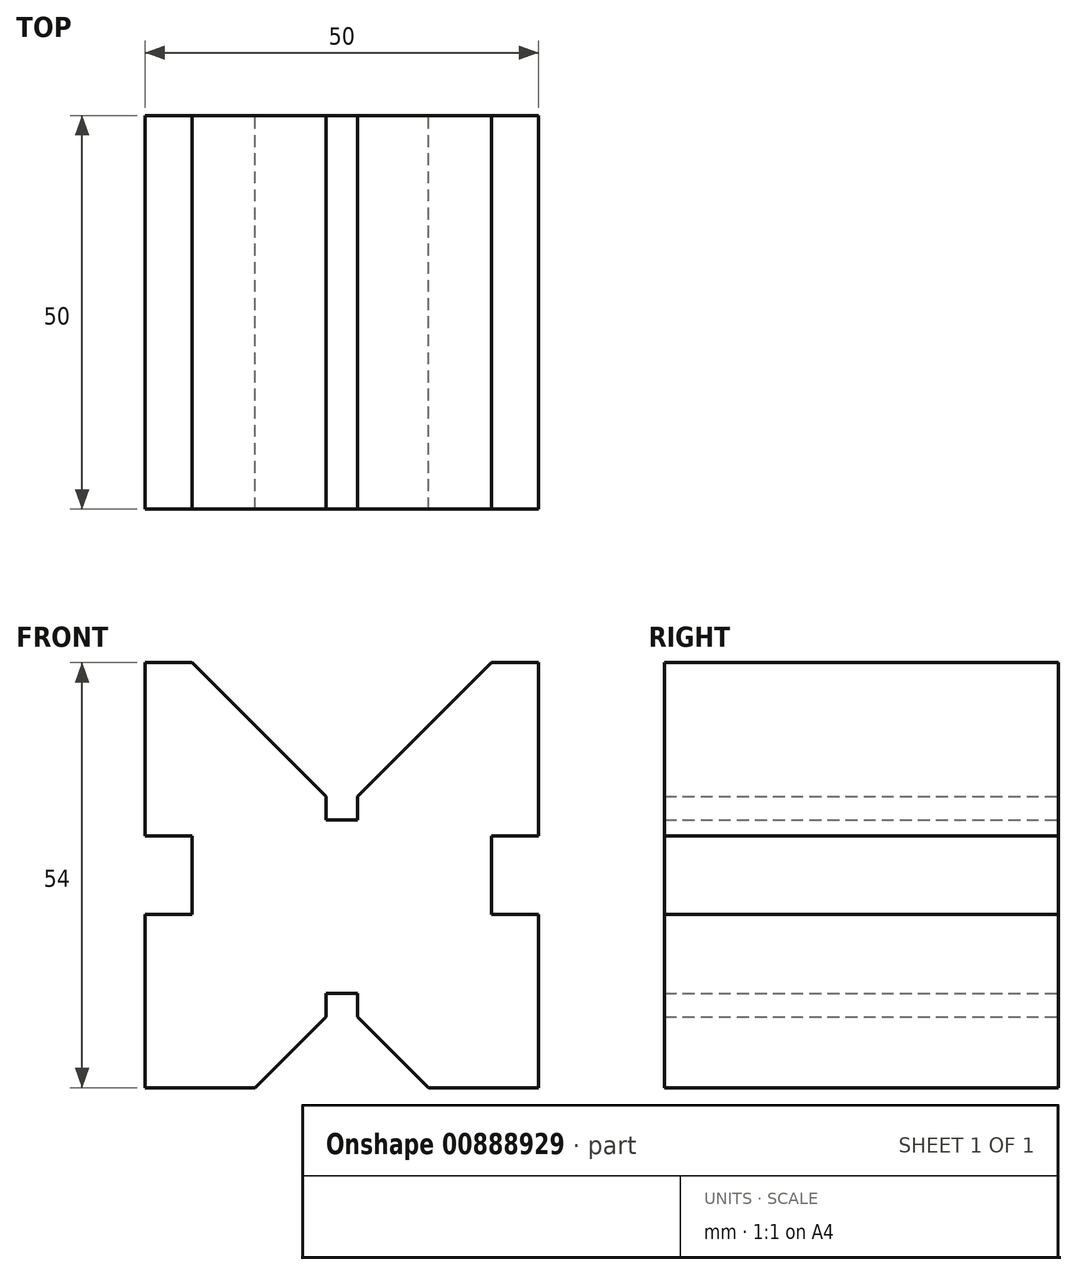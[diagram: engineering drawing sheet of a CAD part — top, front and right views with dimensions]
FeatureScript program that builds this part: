
annotation { "Feature Type Name" : "Feature", "Feature Type Description" : "" }
export const myFeature = defineFeature(function(context is Context, id is Id, definition is map)
    precondition{}
    {
        {
            var Q0;
            Q0=qCreatedBy(makeId("Front.planeOp"),FACE);
            var sketch = newSketch(context, id + "F0", { "sketchPlane" : qUnion([Q0])});
            skLineSegment(sketch, "E0", {"start": v(-6, 54) * mm, "end": v(0, 54) * mm});
            skLineSegment(sketch, "E1", {"start": v(0, 54) * mm, "end": v(0, 32) * mm});
            skLineSegment(sketch, "E2", {"start": v(0, 32) * mm, "end": v(-6, 32) * mm});
            skLineSegment(sketch, "E3", {"start": v(-6, 32) * mm, "end": v(-6, 22) * mm});
            skLineSegment(sketch, "E4", {"start": v(-6, 22) * mm, "end": v(0, 22) * mm});
            skLineSegment(sketch, "E5", {"start": v(0, 22) * mm, "end": v(0, 0) * mm});
            skLineSegment(sketch, "E6", {"start": v(0, 0) * mm, "end": v(-14, 0) * mm});
            skLineSegment(sketch, "E7", {"start": v(-14, 0) * mm, "end": v(-23, 9) * mm});
            skLineSegment(sketch, "E8", {"start": v(-23, 9) * mm, "end": v(-23, 12) * mm});
            skLineSegment(sketch, "E9", {"start": v(-23, 12) * mm, "end": v(-25, 12) * mm});
            skLineSegment(sketch, "E10", {"start": v(-25, 12) * mm, "end": v(-25, 34) * mm, "construction": true});
            skLineSegment(sketch, "E11", {"start": v(-25, 34) * mm, "end": v(-23, 34) * mm});
            skLineSegment(sketch, "E12", {"start": v(-23, 34) * mm, "end": v(-23, 37) * mm});
            skLineSegment(sketch, "E13", {"start": v(-23, 37) * mm, "end": v(-6, 54) * mm});
            skLineSegment(sketch, "E14.MirrorCS", {"start": v(-25, 34) * mm, "end": v(-27, 34) * mm});
            skLineSegment(sketch, "E15.MirrorCS", {"start": v(-27, 9) * mm, "end": v(-27, 12) * mm});
            skLineSegment(sketch, "E16.MirrorCS", {"start": v(-27, 34) * mm, "end": v(-27, 37) * mm});
            skLineSegment(sketch, "E17.MirrorCS", {"start": v(-27, 12) * mm, "end": v(-25, 12) * mm});
            skLineSegment(sketch, "E18.MirrorCS", {"start": v(-27, 37) * mm, "end": v(-44, 54) * mm});
            skLineSegment(sketch, "E19.MirrorCS", {"start": v(-50, 22) * mm, "end": v(-50, 0) * mm});
            skLineSegment(sketch, "E20.MirrorCS", {"start": v(-50, 0) * mm, "end": v(-36, 0) * mm});
            skLineSegment(sketch, "E21.MirrorCS", {"start": v(-44, 32) * mm, "end": v(-44, 22) * mm});
            skLineSegment(sketch, "E22.MirrorCS", {"start": v(-44, 54) * mm, "end": v(-50, 54) * mm});
            skLineSegment(sketch, "E23.MirrorCS", {"start": v(-36, 0) * mm, "end": v(-27, 9) * mm});
            skLineSegment(sketch, "E24.MirrorCS", {"start": v(-50, 32) * mm, "end": v(-44, 32) * mm});
            skLineSegment(sketch, "E25.MirrorCS", {"start": v(-50, 54) * mm, "end": v(-50, 32) * mm});
            skLineSegment(sketch, "E26.MirrorCS", {"start": v(-44, 22) * mm, "end": v(-50, 22) * mm});
            skSolve(sketch);
        }
        {
            var Q0;
            Q0=makeQuery(id+"F0.imprint","IMPRINT",FACE,{"disambiguationData":[TD([[makeQuery(id+"F0.imprint","IMPRINT",EDGE,{"derivedFrom":sQuery(id+"F0.wireOp",EDGE,"E0")}),-1.0]])]});
            extrude(context, id + "F1", {"entities" : qUnion([Q0]), "depth" : 50 * mm, "offsetDistance" : 25 * mm});
        }
    });
